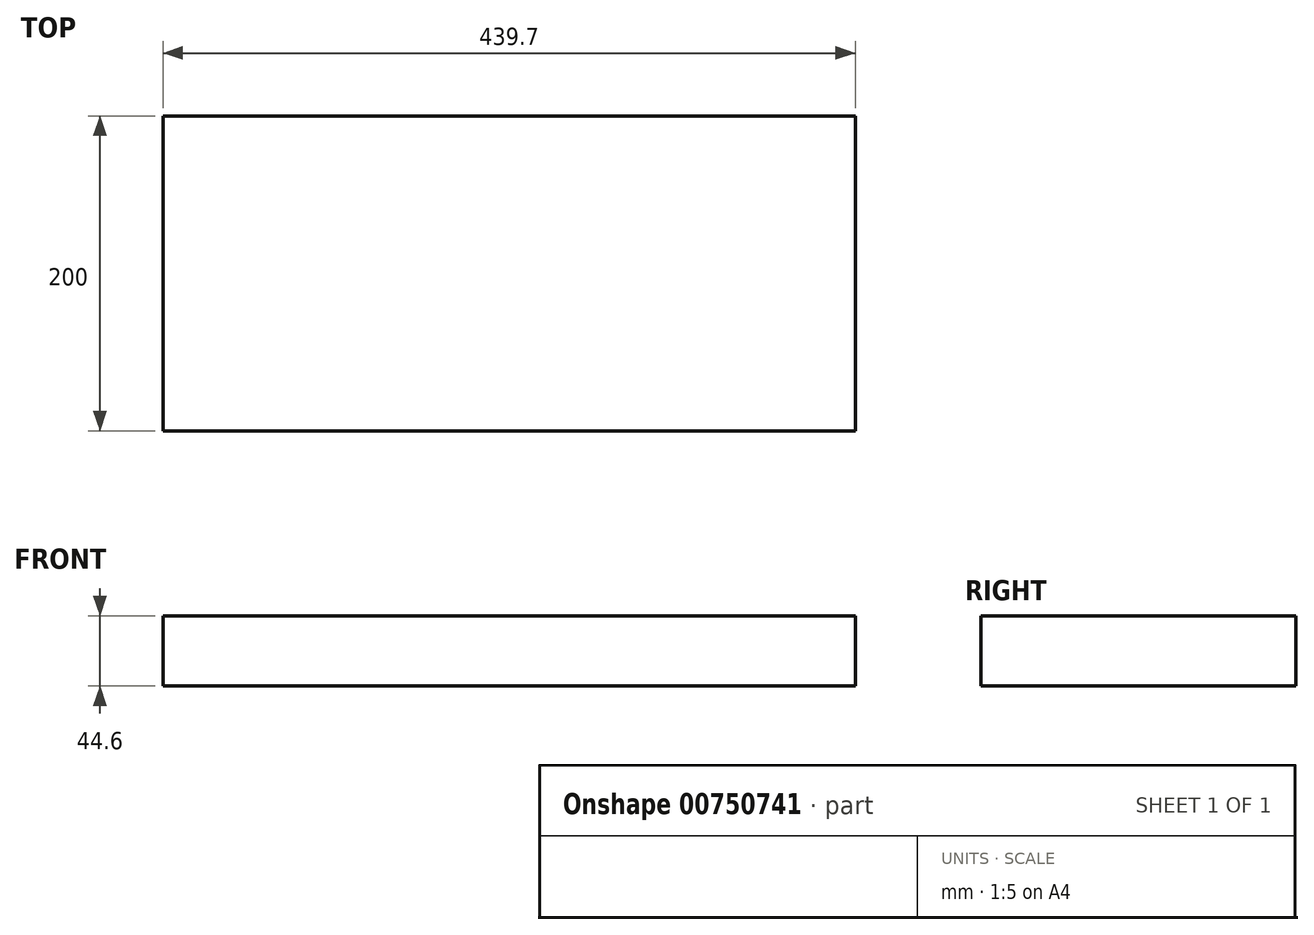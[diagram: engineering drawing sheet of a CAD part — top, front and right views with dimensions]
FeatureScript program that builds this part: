
annotation { "Feature Type Name" : "Feature", "Feature Type Description" : "" }
export const myFeature = defineFeature(function(context is Context, id is Id, definition is map)
    precondition{}
    {
        {
            var Q0;
            Q0=qCreatedBy(makeId("Top.planeOp"),FACE);
            var sketch = newSketch(context, id + "F0", { "sketchPlane" : qUnion([Q0])});
            skLineSegment(sketch, "E0.bottom", {"start": v(219.85, -100) * mm, "end": v(-219.85, -100) * mm});
            skLineSegment(sketch, "E0.top", {"start": v(219.85, 100) * mm, "end": v(-219.85, 100) * mm});
            skLineSegment(sketch, "E0.left", {"start": v(219.85, -100) * mm, "end": v(219.85, 100) * mm});
            skLineSegment(sketch, "E0.right", {"start": v(-219.85, -100) * mm, "end": v(-219.85, 100) * mm});
            skPoint(sketch, "E0.middle", {"position": v(0, 0) * mm});
            skSolve(sketch);
        }
        {
            var Q0;
            Q0 = qSketchRegion(id + "F0", true);
            extrude(context, id + "F1", {"entities" : qUnion([Q0]), "depth" : 44.6 * mm, "offsetDistance" : 25 * mm});
        }
    });
